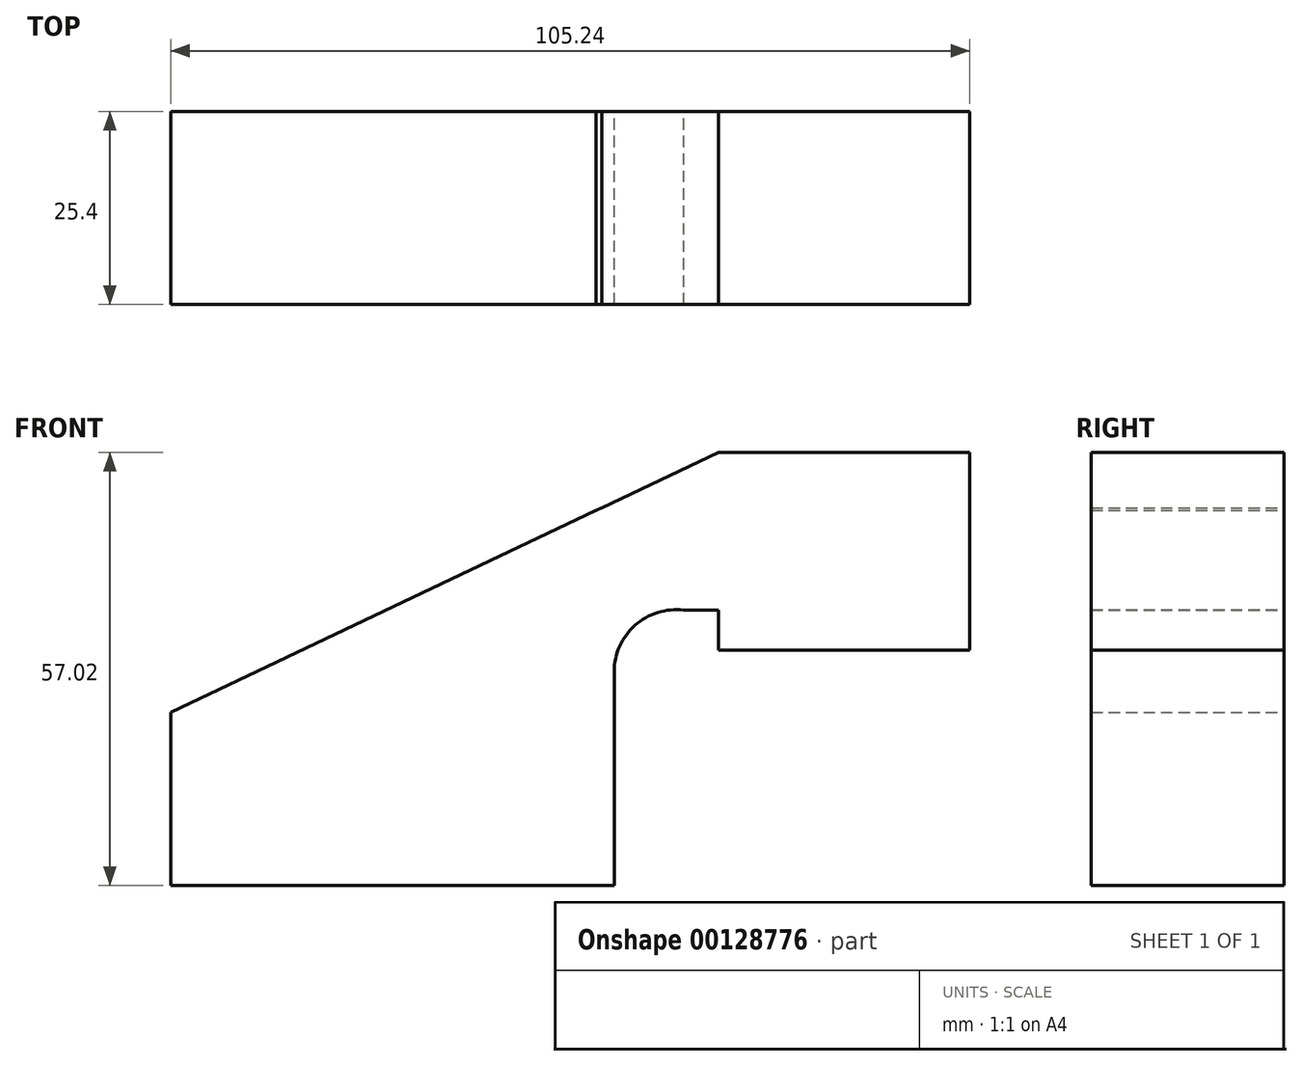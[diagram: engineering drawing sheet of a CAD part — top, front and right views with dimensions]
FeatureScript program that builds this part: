
annotation { "Feature Type Name" : "Feature", "Feature Type Description" : "" }
export const myFeature = defineFeature(function(context is Context, id is Id, definition is map)
    precondition{}
    {
        {
            var Q0;
            Q0=qCreatedBy(makeId("Front.planeOp"),FACE);
            var sketch = newSketch(context, id + "F0", { "sketchPlane" : qUnion([Q0])});
            skLineSegment(sketch, "E0.bottom", {"start": v(-29.21, -11.4) * mm, "end": v(29.21, -11.4) * mm});
            skLineSegment(sketch, "E0.top", {"start": v(-29.21, 11.4) * mm, "end": v(29.21, 11.4) * mm});
            skLineSegment(sketch, "E0.left", {"start": v(-29.21, -11.4) * mm, "end": v(-29.21, 11.4) * mm});
            skLineSegment(sketch, "E0.right", {"start": v(29.21, -11.4) * mm, "end": v(29.21, 11.4) * mm});
            skPoint(sketch, "E0.middle", {"position": v(0, 0) * mm});
            skLineSegment(sketch, "E1.bottom", {"start": v(76.03, 19.57) * mm, "end": v(42.94, 19.57) * mm});
            skLineSegment(sketch, "E1.top", {"start": v(76.03, 45.62) * mm, "end": v(42.94, 45.62) * mm});
            skLineSegment(sketch, "E1.left", {"start": v(76.03, 19.57) * mm, "end": v(76.03, 45.62) * mm});
            skLineSegment(sketch, "E1.right", {"start": v(42.94, 19.57) * mm, "end": v(42.94, 45.62) * mm});
            skPoint(sketch, "E1.middle", {"position": v(59.49, 32.6) * mm});
            skLineSegment(sketch, "E2", {"start": v(29.21, 11.4) * mm, "end": v(29.21, 16.76) * mm});
            skArc(sketch, "E3", {"start": v(29.21, 16.76) * mm, "mid": v(31.97, 22.87) * mm, "end": v(38.37, 24.85) * mm});
            skLineSegment(sketch, "E4", {"start": v(38.37, 24.85) * mm, "end": v(59.49, 24.85) * mm});
            skPoint(sketch, "E4.endSnap0", {"position": v(59.49, 19.57) * mm});
            skLineSegment(sketch, "E5.0", {"start": v(39.07, 40.4) * mm, "end": v(59.49, 40.4) * mm});
            skArc(sketch, "E5.1", {"start": v(13.68, 16.76) * mm, "mid": v(21.23, 34.1) * mm, "end": v(39.07, 40.4) * mm});
            skLineSegment(sketch, "E5.2", {"start": v(13.68, 11.4) * mm, "end": v(13.68, 16.76) * mm});
            skLineSegment(sketch, "E6", {"start": v(59.49, 45.62) * mm, "end": v(59.49, 19.57) * mm});
            skFitSpline(sketch, "E7", {"points": [v(-29.21, 11.4) * mm, v(42.94, 45.62) * mm], "startDerivative": vector(72.16, 34.22) * mm, "endDerivative": vector(72.16, 34.22) * mm});
            skSolve(sketch);
        }
        {
            var Q0;
            Q0 = qSketchRegion(id + "F0", true);
            extrude(context, id + "F1", {"entities" : qUnion([Q0]), "depth" : 25.4 * mm});
        }
    });
